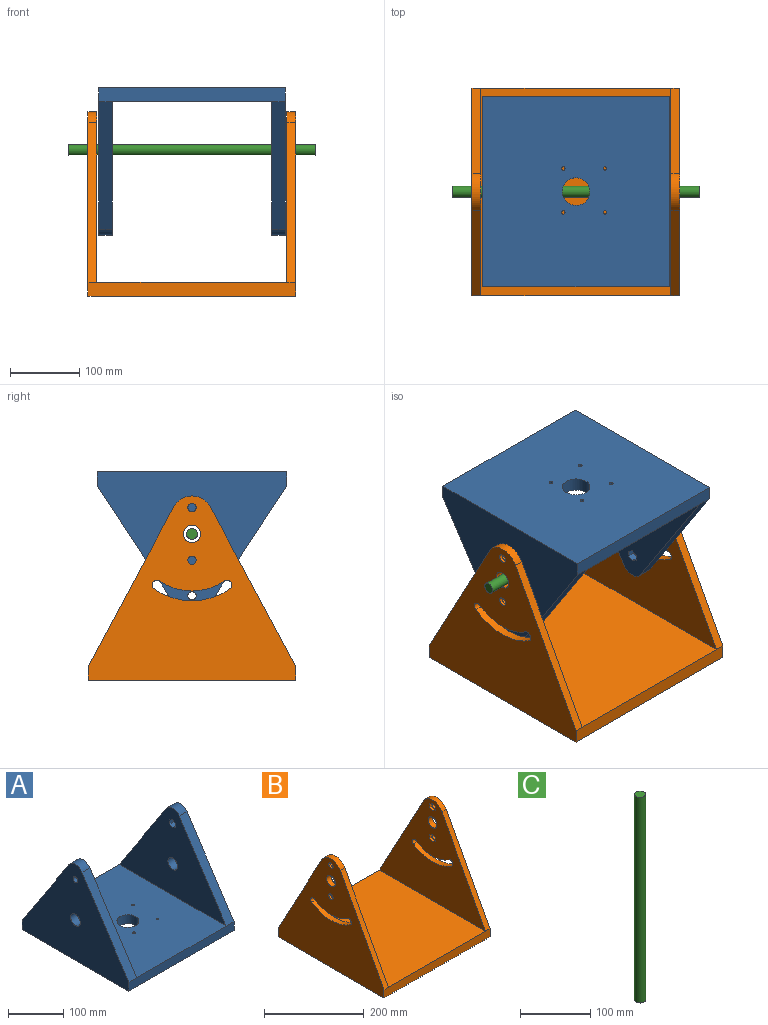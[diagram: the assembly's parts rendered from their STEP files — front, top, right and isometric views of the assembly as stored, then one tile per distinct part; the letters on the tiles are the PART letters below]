
ASSEMBLY  parts=3 mates=2
PART A: 37 faces, bbox 270x274.6x213.5 mm
  f0: plane 274.6x230mm, normal (0,0,1), area 61822.8mm2, adj f2,f4,f5,f6,f32,f33,f34,f35
  f1: plane 274.6x270mm, normal (0,0,-1), area 72806.8mm2, adj f5,f6,f7,f8,f32,f33,f34,f35
  f2: plane 274.6x193.45mm, normal (1,0,0), area 27932.2mm2, adj f0,f13,f14,f15,f17,f25,f26,f27
  f3: cylinder r=6mm len=12mm, axis (1,0,0), area 377mm2, adj f7,f31
  f4: plane 274.6x193.45mm, normal (-1,0,0), area 27932.2mm2, adj f0,f9,f10,f11,f16,f18,f19,f20
  f5: plane 270x20mm, normal (0,1,0), area 5400mm2, adj f0,f1,f7,f8,f11,f13
  f6: plane 270x20mm, normal (0,-1,0), area 5400mm2, adj f0,f1,f7,f8,f10,f14
  f7: plane 274.6x213.45mm, normal (-1,0,0), area 33505.9mm2, adj f1,f3,f5,f6,f13,f14,f15,f17
  f8: plane 274.6x213.45mm, normal (1,0,0), area 33505.9mm2, adj f1,f5,f6,f9,f10,f11,f12,f16
  f9: cylinder r=20mm len=33.48mm, axis (1,0,0), area 793.4mm2, adj f4,f8,f10,f11
  f10: plane 184.4x120.56mm, normal (0,-0.84,0.55), area 4406.2mm2, adj f4,f6,f8,f9
  f11: plane 184.4x120.56mm, normal (0,0.84,0.55), area 4406.2mm2, adj f4,f5,f8,f9
  f12: cylinder r=6mm len=12mm, axis (1,0,0), area 377mm2, adj f8,f24
  f13: plane 184.4x120.56mm, normal (0,0.84,0.55), area 4406.2mm2, adj f2,f5,f7,f15
  f14: plane 184.4x120.56mm, normal (0,-0.84,0.55), area 4406.2mm2, adj f2,f6,f7,f15
  f15: cylinder r=20mm len=33.48mm, axis (1,0,0), area 793.4mm2, adj f2,f7,f13,f14
  f16: cylinder r=12.5mm len=25mm, axis (1,0,0), area 1570.8mm2, adj f4,f8
  f17: cylinder r=12.5mm len=25mm, axis (1,0,0), area 1570.8mm2, adj f2,f7
  f18: plane 10x7.5mm, normal (0,0.5,0.87), area 86.6mm2, adj f4,f19,f23,f24
  f19: plane 10x7.5mm, normal (0,-0.5,0.87), area 86.6mm2, adj f4,f18,f20,f24
  f20: plane 10x8.66mm, normal (0,-1,0), area 86.6mm2, adj f4,f19,f21,f24
  f21: plane 10x7.5mm, normal (0,-0.5,-0.87), area 86.6mm2, adj f4,f20,f22,f24
  f22: plane 10x7.5mm, normal (0,0.5,-0.87), area 86.6mm2, adj f4,f21,f23,f24
  f23: plane 10x8.66mm, normal (0,1,0), area 86.6mm2, adj f4,f18,f22,f24
  f24: plane 17.32x15mm, normal (-1,0,0), area 81.8mm2, adj f12,f18,f19,f20,f21,f22,f23
  f25: plane 10x7.5mm, normal (0,0.5,0.87), area 86.6mm2, adj f2,f26,f30,f31
  f26: plane 10x7.5mm, normal (0,-0.5,0.87), area 86.6mm2, adj f2,f25,f27,f31
  f27: plane 10x8.66mm, normal (0,-1,0), area 86.6mm2, adj f2,f26,f28,f31
  f28: plane 10x7.5mm, normal (0,-0.5,-0.87), area 86.6mm2, adj f2,f27,f29,f31
  f29: plane 10x7.5mm, normal (0,0.5,-0.87), area 86.6mm2, adj f2,f28,f30,f31
  f30: plane 10x8.66mm, normal (0,1,0), area 86.6mm2, adj f2,f25,f29,f31
  f31: plane 17.32x15mm, normal (1,0,0), area 81.8mm2, adj f3,f25,f26,f27,f28,f29,f30
  f32: cylinder r=20mm len=40mm, axis (0,0,1), area 2513.3mm2, adj f0,f1
  f33: cylinder r=2.5mm len=20mm, axis (0,0,1), area 314.2mm2, adj f0,f1
  f34: cylinder r=2.5mm len=20mm, axis (0,0,1), area 314.2mm2, adj f0,f1
  f35: cylinder r=2.5mm len=20mm, axis (0,0,1), area 314.2mm2, adj f0,f1
  f36: cylinder r=2.5mm len=20mm, axis (0,0,1), area 314.2mm2, adj f0,f1
PART B: 56 faces, bbox 300x300x266.5 mm
  f0: plane 300x246.47mm, normal (-1,0,0), area 38749.7mm2, adj f8,f10,f12,f15,f16,f34,f35,f36
  f1: plane 300x246.47mm, normal (1,0,0), area 38749.7mm2, adj f8,f11,f13,f14,f17,f20,f21,f22
  f2: plane 300x266.47mm, normal (-1,0,0), area 44913.2mm2, adj f6,f7,f9,f11,f13,f14,f17,f18
  f3: plane 300x266.47mm, normal (1,0,0), area 44913.2mm2, adj f4,f5,f6,f7,f9,f10,f12,f15
  f4: cylinder r=6mm len=12mm, axis (-1,0,0), area 290.3mm2, adj f3,f47
  f5: cylinder r=6mm len=12mm, axis (-1,0,0), area 290.3mm2, adj f3,f40
  f6: plane 300x20mm, normal (0,1,0), area 6000mm2, adj f2,f3,f8,f9,f12,f13
  f7: plane 300x20mm, normal (0,-1,0), area 6000mm2, adj f2,f3,f8,f9,f10,f11
  f8: plane 300x274.6mm, normal (0,0,1), area 82380mm2, adj f0,f1,f6,f7
  f9: plane 300x300mm, normal (0,0,-1), area 90000mm2, adj f2,f3,f6,f7
  f10: plane 230.64x123.56mm, normal (0,-0.88,0.47), area 3322.9mm2, adj f0,f3,f7,f15
  f11: plane 230.64x123.56mm, normal (0,-0.88,0.47), area 3322.9mm2, adj f1,f2,f7,f14
  f12: plane 230.64x123.56mm, normal (0,0.88,0.47), area 3322.9mm2, adj f0,f3,f6,f15
  f13: plane 230.64x123.56mm, normal (0,0.88,0.47), area 3322.9mm2, adj f1,f2,f6,f14
  f14: cylinder r=30mm len=52.89mm, axis (-1,0,0), area 822.2mm2, adj f1,f2,f11,f13
  f15: cylinder r=30mm len=52.89mm, axis (-1,0,0), area 822.2mm2, adj f0,f3,f10,f12
  f16: cylinder r=12.5mm len=25mm, axis (-1,0,0), area 997.5mm2, adj f0,f3
  f17: cylinder r=12.5mm len=25mm, axis (-1,0,0), area 997.5mm2, adj f1,f2
  f18: cylinder r=6mm len=12mm, axis (-1,0,0), area 188.5mm2, adj f2,f33
  f19: cylinder r=6mm len=12mm, axis (-1,0,0), area 188.5mm2, adj f2,f26
  f20: plane 7.7x7.5mm, normal (0,-0.5,0.87), area 66.7mm2, adj f1,f21,f25,f26
  f21: plane 7.7x7.5mm, normal (0,0.5,0.87), area 66.7mm2, adj f1,f20,f22,f26
  f22: plane 8.66x7.7mm, normal (0,1,0), area 66.7mm2, adj f1,f21,f23,f26
  f23: plane 7.7x7.5mm, normal (0,0.5,-0.87), area 66.7mm2, adj f1,f22,f24,f26
  f24: plane 7.7x7.5mm, normal (0,-0.5,-0.87), area 66.7mm2, adj f1,f23,f25,f26
  f25: plane 8.66x7.7mm, normal (0,-1,0), area 66.7mm2, adj f1,f20,f24,f26
  f26: plane 17.32x15mm, normal (1,0,0), area 81.8mm2, adj f19,f20,f21,f22,f23,f24,f25
  f27: plane 7.7x7.5mm, normal (0,0.5,-0.87), area 66.7mm2, adj f1,f28,f32,f33
  f28: plane 7.7x7.5mm, normal (0,-0.5,-0.87), area 66.7mm2, adj f1,f27,f29,f33
  f29: plane 8.66x7.7mm, normal (0,-1,0), area 66.7mm2, adj f1,f28,f30,f33
  f30: plane 7.7x7.5mm, normal (0,-0.5,0.87), area 66.7mm2, adj f1,f29,f31,f33
  f31: plane 7.7x7.5mm, normal (0,0.5,0.87), area 66.7mm2, adj f1,f30,f32,f33
  f32: plane 8.66x7.7mm, normal (0,1,0), area 66.7mm2, adj f1,f27,f31,f33
  f33: plane 17.32x15mm, normal (1,0,0), area 81.8mm2, adj f18,f27,f28,f29,f30,f31,f32
  f34: plane 7.5x5mm, normal (0,-0.5,0.87), area 43.3mm2, adj f0,f35,f39,f40
  f35: plane 7.5x5mm, normal (0,0.5,0.87), area 43.3mm2, adj f0,f34,f36,f40
  f36: plane 8.66x5mm, normal (0,1,0), area 43.3mm2, adj f0,f35,f37,f40
  f37: plane 7.5x5mm, normal (0,0.5,-0.87), area 43.3mm2, adj f0,f36,f38,f40
  f38: plane 7.5x5mm, normal (0,-0.5,-0.87), area 43.3mm2, adj f0,f37,f39,f40
  f39: plane 8.66x5mm, normal (0,-1,0), area 43.3mm2, adj f0,f34,f38,f40
  f40: plane 17.32x15mm, normal (-1,0,0), area 81.8mm2, adj f5,f34,f35,f36,f37,f38,f39
  f41: plane 7.5x5mm, normal (0,0.5,-0.87), area 43.3mm2, adj f0,f42,f46,f47
  f42: plane 7.5x5mm, normal (0,-0.5,-0.87), area 43.3mm2, adj f0,f41,f43,f47
  f43: plane 8.66x5mm, normal (0,-1,0), area 43.3mm2, adj f0,f42,f44,f47
  f44: plane 7.5x5mm, normal (0,-0.5,0.87), area 43.3mm2, adj f0,f43,f45,f47
  f45: plane 7.5x5mm, normal (0,0.5,0.87), area 43.3mm2, adj f0,f44,f46,f47
  f46: plane 8.66x5mm, normal (0,1,0), area 43.3mm2, adj f0,f41,f45,f47
  f47: plane 17.32x15mm, normal (-1,0,0), area 81.8mm2, adj f4,f41,f42,f43,f44,f45,f46
  f48: cylinder r=96.45mm len=109.18mm, axis (-1,0,0), area 1473.9mm2, adj f0,f3,f54,f55
  f49: cylinder r=82.45mm len=93.33mm, axis (-1,0,0), area 1260mm2, adj f0,f3,f54,f55
  f50: cylinder r=82.45mm len=93.33mm, axis (-1,0,0), area 1260mm2, adj f1,f2,f52,f53
  f51: cylinder r=96.45mm len=109.18mm, axis (-1,0,0), area 1473.9mm2, adj f1,f2,f52,f53
  f52: cylinder r=7mm len=12.77mm, axis (-1,0,0), area 279.3mm2, adj f1,f2,f50,f51
  f53: cylinder r=7mm len=12.77mm, axis (-1,0,0), area 279.3mm2, adj f1,f2,f50,f51
  f54: cylinder r=7mm len=12.77mm, axis (-1,0,0), area 279.3mm2, adj f0,f3,f48,f49
  f55: cylinder r=7mm len=12.77mm, axis (-1,0,0), area 279.3mm2, adj f0,f3,f48,f49
PART C: 3 faces, bbox 15.9x15.9x358 mm
  f0: cylinder r=7.94mm len=358mm, axis (0,0,-1), area 17854.5mm2, adj f1,f2
  f1: plane 15.88x15.88mm, normal (0,0,1), area 197.9mm2, adj f0
  f2: plane 15.88x15.88mm, normal (0,0,-1), area 197.9mm2, adj f0
PLACE A rot(axis=(1,0,0),180deg) t=(-18.25,87.38,346.52)mm
PLACE B t=(-17.15,87.85,45.05)mm
PLACE C rot(axis=(0,-1,0),90deg) t=(163.95,65.39,256.52)mm
MATE revolute C.f0 <-> B.f16  axis (-1,0,0) through (-194.05,65.39,256.52)mm
MATE fastened A.f16 <-> C.f0  axis (1,0,0) through (-140.05,65.39,256.52)mm
